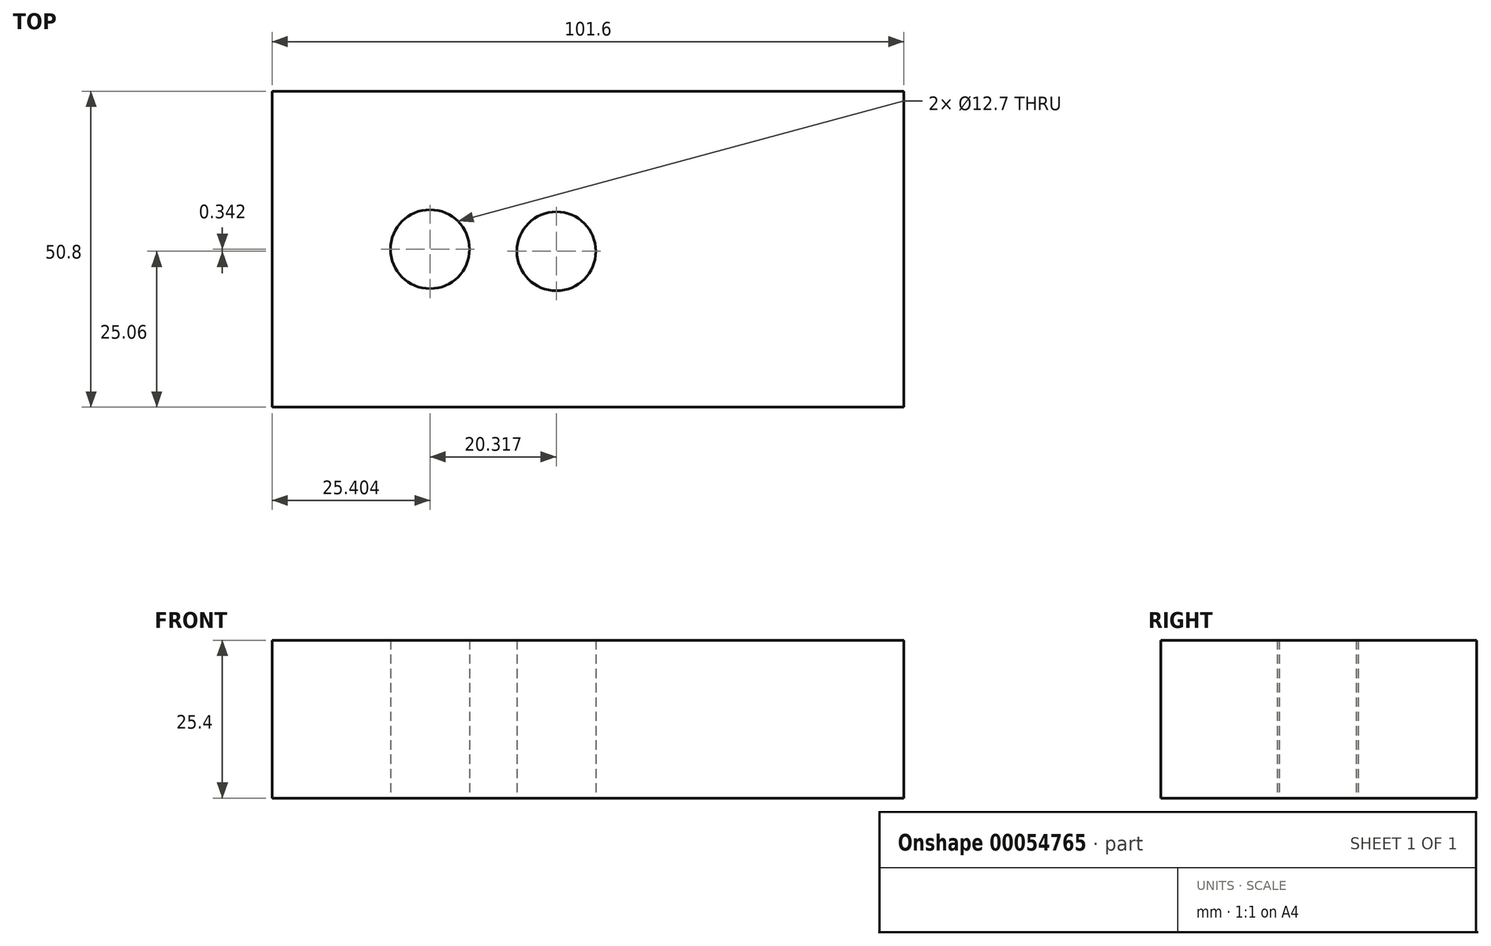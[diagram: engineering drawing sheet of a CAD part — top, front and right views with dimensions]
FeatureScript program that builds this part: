
annotation { "Feature Type Name" : "Feature", "Feature Type Description" : "" }
export const myFeature = defineFeature(function(context is Context, id is Id, definition is map)
    precondition{}
    {
        {
            var Q0;
            Q0=qCreatedBy(makeId("Top.planeOp"),FACE);
            var sketch = newSketch(context, id + "F0", { "sketchPlane" : qUnion([Q0])});
            skLineSegment(sketch, "E0.bottom", {"start": v(-51.66, 27.15) * mm, "end": v(49.94, 27.15) * mm});
            skLineSegment(sketch, "E0.top", {"start": v(-51.66, -23.65) * mm, "end": v(49.94, -23.65) * mm});
            skLineSegment(sketch, "E0.left", {"start": v(-51.66, 27.15) * mm, "end": v(-51.66, -23.65) * mm});
            skLineSegment(sketch, "E0.right", {"start": v(49.94, 27.15) * mm, "end": v(49.94, -23.65) * mm});
            skCircle(sketch, "E1", {"center": v(-26.26, 1.75) * mm, "radius": 6.35 * mm});
            skCircle(sketch, "E2", {"center": v(-5.94, 1.41) * mm, "radius": 6.35 * mm});
            skSolve(sketch);
        }
        {
            var Q0;
            Q0=makeQuery(id+"F0.imprint","IMPRINT",FACE,{"disambiguationData":[TD([[makeQuery(id+"F0.imprint","IMPRINT",EDGE,{"derivedFrom":sQuery(id+"F0.wireOp",EDGE,"E0.bottom")}),-1.0]])]});
            extrude(context, id + "F1", {"entities" : qUnion([Q0]), "depth" : 25.4 * mm});
        }
    });
